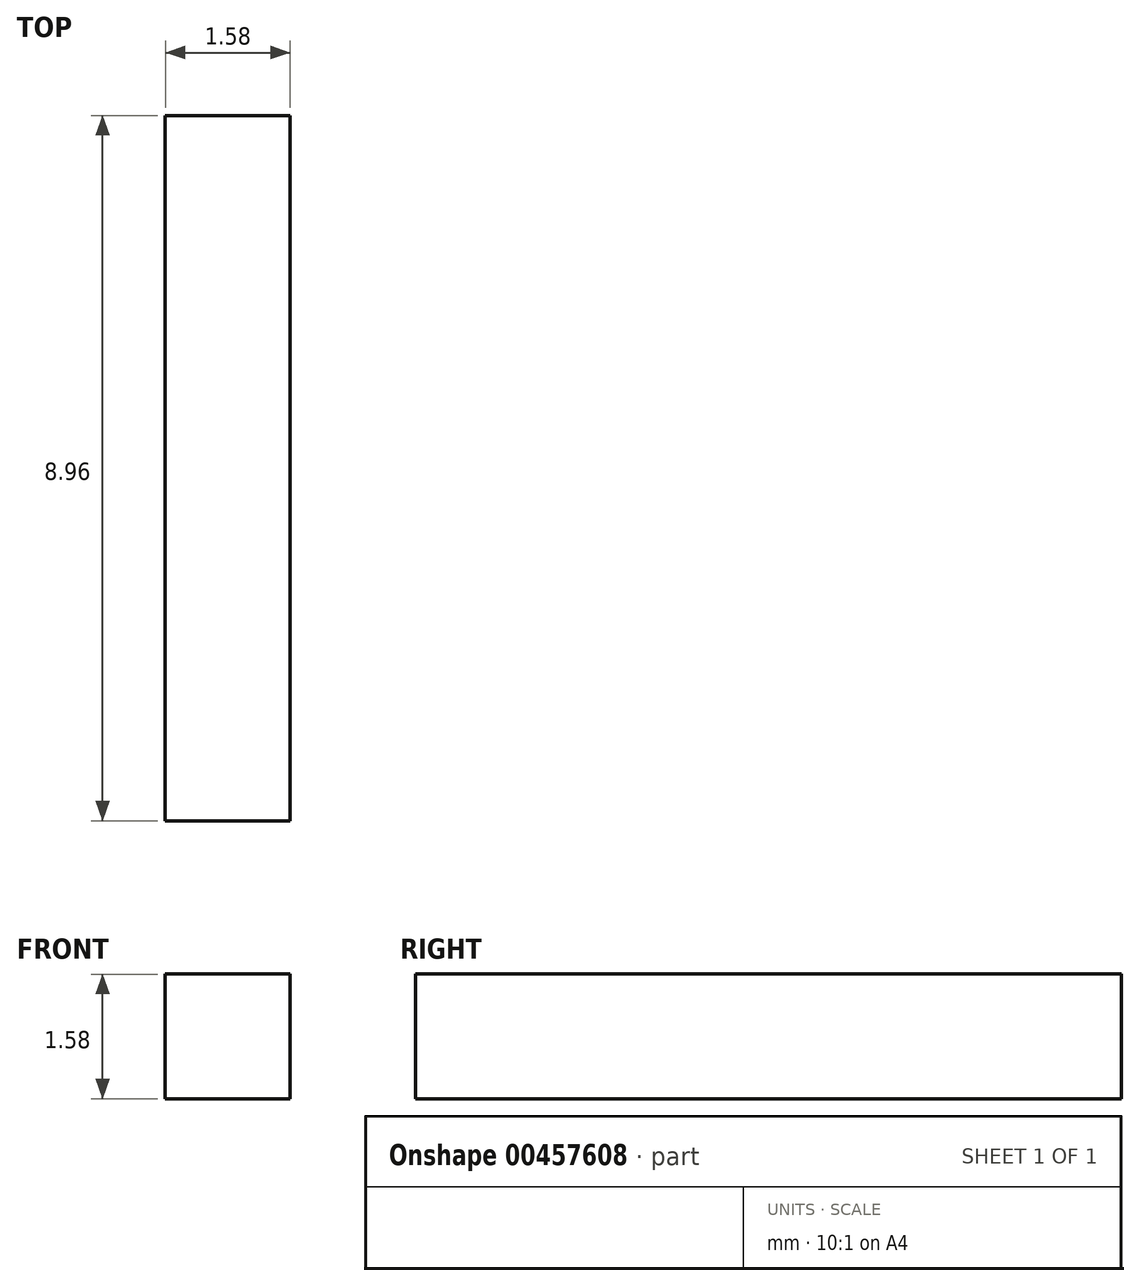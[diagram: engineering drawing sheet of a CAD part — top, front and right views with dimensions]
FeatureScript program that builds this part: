
annotation { "Feature Type Name" : "Feature", "Feature Type Description" : "" }
export const myFeature = defineFeature(function(context is Context, id is Id, definition is map)
    precondition{}
    {
        {
            var Q0;
            Q0=qCreatedBy(makeId("Front.planeOp"),FACE);
            var sketch = newSketch(context, id + "F0", { "sketchPlane" : qUnion([Q0])});
            skLineSegment(sketch, "E0.bottom", {"start": v(-0.8, 0.8) * mm, "end": v(0.8, 0.8) * mm});
            skLineSegment(sketch, "E0.top", {"start": v(-0.8, -0.8) * mm, "end": v(0.8, -0.8) * mm});
            skLineSegment(sketch, "E0.left", {"start": v(-0.8, 0.8) * mm, "end": v(-0.8, -0.8) * mm});
            skLineSegment(sketch, "E0.right", {"start": v(0.8, 0.8) * mm, "end": v(0.8, -0.8) * mm});
            skPoint(sketch, "E0.middle", {"position": v(0, 0) * mm});
            skSolve(sketch);
        }
        {
            var Q0;
            Q0 = qSketchRegion(id + "F0", true);
            extrude(context, id + "F1", {"entities" : qUnion([Q0]), "depth" : 8.96 * mm});
        }
    });
